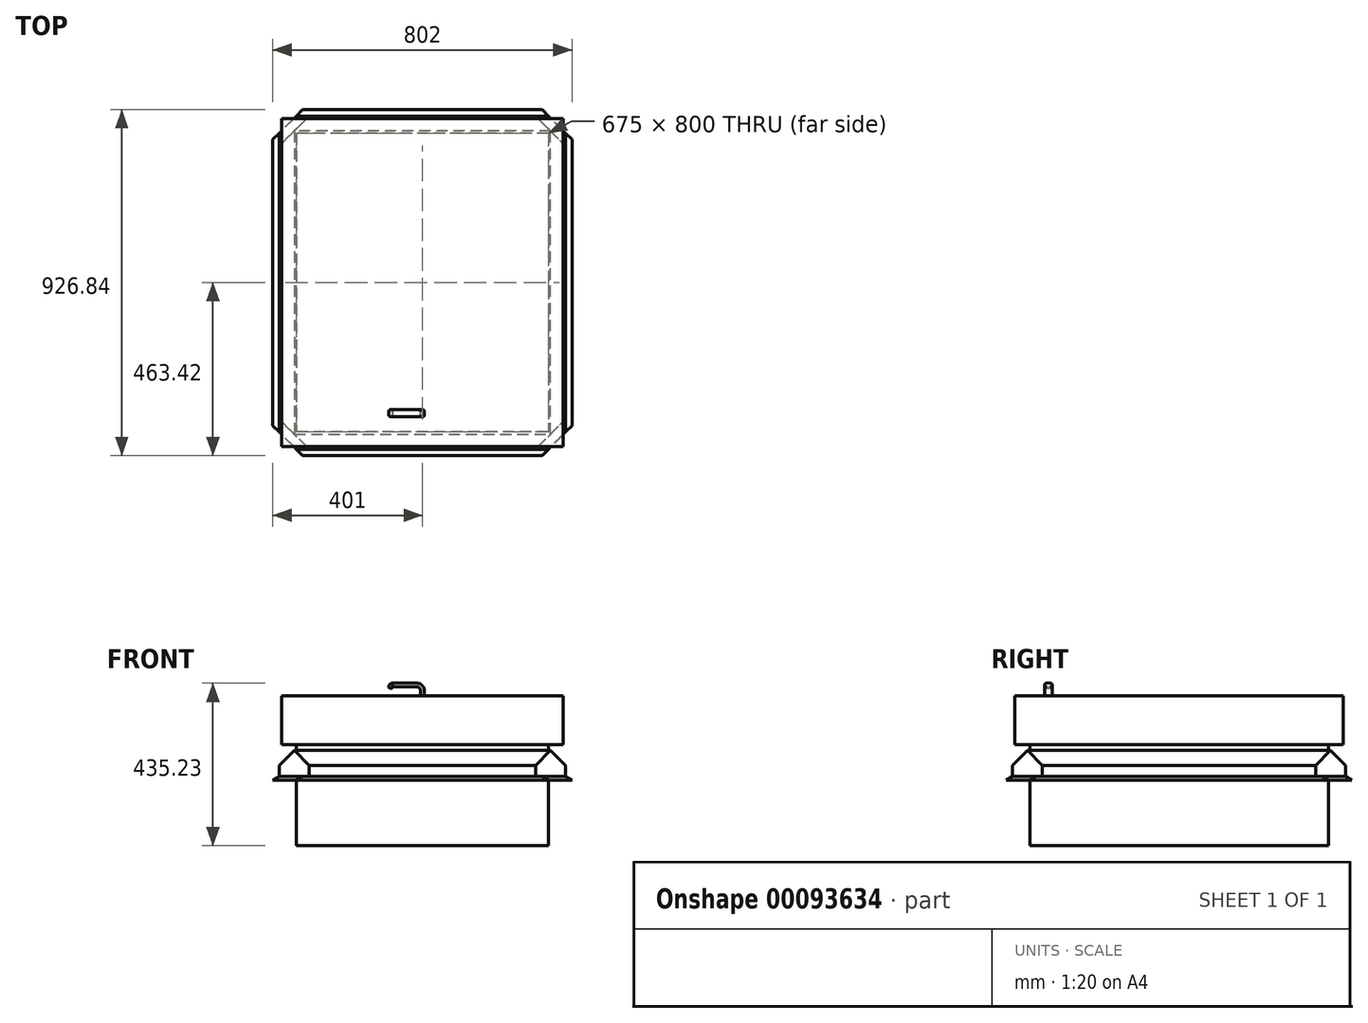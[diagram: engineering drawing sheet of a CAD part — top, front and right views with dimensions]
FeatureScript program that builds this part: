
annotation { "Feature Type Name" : "Feature", "Feature Type Description" : "" }
export const myFeature = defineFeature(function(context is Context, id is Id, definition is map)
    precondition{}
    {
        {
            var Q0;
            Q0=qCreatedBy(makeId("Top.planeOp"),FACE);
            var sketch = newSketch(context, id + "F0", { "sketchPlane" : qUnion([Q0])});
            skLineSegment(sketch, "E0.top", {"start": v(-337.5, 400) * mm, "end": v(337.5, 400) * mm});
            skLineSegment(sketch, "E0.left", {"start": v(-337.5, -400) * mm, "end": v(-337.5, 400) * mm});
            skLineSegment(sketch, "E0.right", {"start": v(337.5, -400) * mm, "end": v(337.5, 400) * mm});
            skPoint(sketch, "E0.middle", {"position": v(0, 0) * mm});
            skPoint(sketch, "E1.endSnap0", {"position": v(-337.5, 0) * mm});
            skLineSegment(sketch, "E2", {"start": v(-337.5, -400) * mm, "end": v(337.5, -400) * mm});
            skPoint(sketch, "E3.start.orphan", {"position": v(-337.5, -825.74) * mm});
            skSolve(sketch);
        }
        {
            var Q0;
            Q0 = qSketchRegion(id + "F0", true);
            extrude(context, id + "F1", {"entities" : qUnion([Q0]), "depth" : 270 * mm});
        }
        {
            var Q0;
            Q0=makeQuery(id+"F1.opExtrude","CAP_FACE",FACE,{"disambiguationData":[OSD([sQuery(id+"F0.wireOp",EDGE,"E0.bottom"),sQuery(id+"F0.wireOp",EDGE,"E0.top"),sQuery(id+"F0.wireOp",EDGE,"E0.left"),sQuery(id+"F0.wireOp",EDGE,"E0.right")])],"isStart":false});
            var sketch = newSketch(context, id + "F2", { "sketchPlane" : qUnion([Q0])});
            skLineSegment(sketch, "E4.top", {"start": v(-377.5, 440) * mm, "end": v(377.5, 440) * mm});
            skPoint(sketch, "E4.middle", {"position": v(0, 0) * mm});
            skPoint(sketch, "E5.orphan", {"position": v(377.5, -440) * mm});
            skLineSegment(sketch, "E6", {"start": v(377.5, -440) * mm, "end": v(-377.5, -440) * mm});
            skLineSegment(sketch, "E7", {"start": v(377.5, -440) * mm, "end": v(377.5, 440) * mm});
            skLineSegment(sketch, "E8", {"start": v(-377.5, 440) * mm, "end": v(-377.5, -440) * mm});
            skSolve(sketch);
        }
        {
            var Q0;
            Q0 = qSketchRegion(id + "F2", true);
            extrude(context, id + "F3", {"entities" : qUnion([Q0]), "operationType" : NewBodyOperationType.ADD, "depth" : 131.76 * mm});
        }
        {
            var Q0;
            Q0=makeQuery(id+"F1.opExtrude","CAP_FACE",FACE,{"disambiguationData":[OSD([sQuery(id+"F0.wireOp",EDGE,"E0.bottom"),sQuery(id+"F0.wireOp",EDGE,"E0.top"),sQuery(id+"F0.wireOp",EDGE,"E0.left"),sQuery(id+"F0.wireOp",EDGE,"E0.right")])],"isStart":true});
            var sketch = newSketch(context, id + "F4", { "sketchPlane" : qUnion([Q0])});
            skLineSegment(sketch, "E9.bottom", {"start": v(-401, -463.42) * mm, "end": v(401, -463.42) * mm});
            skLineSegment(sketch, "E9.left", {"start": v(-401, -463.42) * mm, "end": v(-401, 463.42) * mm});
            skPoint(sketch, "E9.middle", {"position": v(0, 0) * mm});
            skLineSegment(sketch, "E10", {"start": v(-401, 463.42) * mm, "end": v(401, 463.42) * mm});
            skLineSegment(sketch, "E11", {"start": v(401, 463.42) * mm, "end": v(401, -463.42) * mm});
            skSolve(sketch);
        }
        {
            var Q0;
            Q0 = qSketchRegion(id + "F4", true);
            extrude(context, id + "F5", {"entities" : qUnion([Q0]), "operationType" : NewBodyOperationType.ADD, "oppositeDirection" : true, "depth" : 185 * mm, "hasSecondDirection" : true, "secondDirectionOppositeDirection" : true, "secondDirectionDepth" : 175 * mm});
        }
        {
            var Q0;
            Q0=makeQuery(id+"F5.opExtrude","CAP_FACE",FACE,{"disambiguationData":[OSD([sQuery(id+"F4.wireOp",EDGE,"E9.bottom"),sQuery(id+"F4.wireOp",EDGE,"E9.top"),sQuery(id+"F4.wireOp",EDGE,"E9.left"),sQuery(id+"F4.wireOp",EDGE,"E9.right")])],"isStart":false});
            var sketch = newSketch(context, id + "F6", { "sketchPlane" : qUnion([Q0])});
            skLineSegment(sketch, "E12.top", {"start": v(-383.5, 446) * mm, "end": v(383.5, 446) * mm});
            skLineSegment(sketch, "E12.left", {"start": v(-383.5, -446) * mm, "end": v(-383.5, 446) * mm});
            skLineSegment(sketch, "E12.right", {"start": v(383.5, -446) * mm, "end": v(383.5, 446) * mm});
            skPoint(sketch, "E12.middle", {"position": v(0, 0) * mm});
            skPoint(sketch, "E13.orphan", {"position": v(383.5, -446) * mm});
            skLineSegment(sketch, "E14", {"start": v(-383.5, -446) * mm, "end": v(383.5, -446) * mm});
            skSolve(sketch);
        }
        {
            var Q0;
            Q0 = qSketchRegion(id + "F6", true);
            extrude(context, id + "F7", {"entities" : qUnion([Q0]), "operationType" : NewBodyOperationType.ADD, "depth" : 70 * mm});
        }
        {
            var Q0;
            Q0=makeQuery(id+"F7.opExtrude","SWEPT_EDGE",EDGE,{"disambiguationData":[OSD([sQuery(id+"F6.wireOp",EDGE,"E12.bottom"),sQuery(id+"F6.wireOp",EDGE,"E12.right")])]});
            var Q1;
            Q1=makeQuery(id+"F7.opExtrude","SWEPT_EDGE",EDGE,{"disambiguationData":[OSD([sQuery(id+"F6.wireOp",EDGE,"E12.top"),sQuery(id+"F6.wireOp",EDGE,"E12.right")])]});
            var Q2;
            Q2=makeQuery(id+"F7.opExtrude","SWEPT_EDGE",EDGE,{"disambiguationData":[OSD([sQuery(id+"F6.wireOp",EDGE,"E12.top"),sQuery(id+"F6.wireOp",EDGE,"E12.left")])]});
            var Q3;
            Q3=makeQuery(id+"F7.opExtrude","SWEPT_EDGE",EDGE,{"disambiguationData":[OSD([sQuery(id+"F6.wireOp",EDGE,"E12.left"),sQuery(id+"F6.wireOp",EDGE,"E14")])]});
            var Q4;
            Q4=makeQuery(id+"F5.opExtrude","SWEPT_EDGE",EDGE,{"disambiguationData":[OSD([sQuery(id+"F4.wireOp",EDGE,"E9.bottom"),sQuery(id+"F4.wireOp",EDGE,"E9.left")])]});
            var Q5;
            Q5=makeQuery(id+"F5.opExtrude","SWEPT_EDGE",EDGE,{"disambiguationData":[OSD([sQuery(id+"F4.wireOp",EDGE,"E9.left"),sQuery(id+"F4.wireOp",EDGE,"E10")])]});
            var Q6;
            Q6=makeQuery(id+"F5.opExtrude","SWEPT_EDGE",EDGE,{"disambiguationData":[OSD([sQuery(id+"F4.wireOp",EDGE,"E9.bottom"),sQuery(id+"F4.wireOp",EDGE,"E11")])]});
            var Q7;
            Q7=makeQuery(id+"F5.opExtrude","SWEPT_EDGE",EDGE,{"disambiguationData":[OSD([sQuery(id+"F4.wireOp",EDGE,"E10"),sQuery(id+"F4.wireOp",EDGE,"E11")])]});
            chamfer(context, id + "F8", {"entities" : qUnion([Q0, Q1, Q2, Q3, Q4, Q5, Q6, Q7]), "width" : 80 * mm, "tangentPropagation" : true});
        }
        {
            var Q0;
            Q0=makeQuery(id+"F7.opExtrude","CAP_EDGE",EDGE,{"disambiguationData":[OSD([sQuery(id+"F6.wireOp",EDGE,"E12.bottom")])],"isStart":false});
            var Q1;
            Q1=makeQuery(id+"F7.opExtrude","CAP_EDGE",EDGE,{"disambiguationData":[OSD([sQuery(id+"F6.wireOp",EDGE,"E12.right")])],"isStart":false});
            var Q2;
            Q2=makeQuery(id+"F7.opExtrude","CAP_EDGE",EDGE,{"disambiguationData":[OSD([sQuery(id+"F6.wireOp",EDGE,"E12.left")])],"isStart":false});
            var Q3;
            Q3=makeQuery(id+"F7.opExtrude","CAP_EDGE",EDGE,{"disambiguationData":[OSD([sQuery(id+"F6.wireOp",EDGE,"E12.top")])],"isStart":false});
            var Q4;
            Q4=makeQuery(id+"F7.opExtrude","CAP_EDGE",EDGE,{"disambiguationData":[OSD([sQuery(id+"F6.wireOp",EDGE,"E14")])],"isStart":false});
            chamfer(context, id + "F9", {"entities" : qUnion([Q0, Q1, Q2, Q3, Q4]), "width" : 40 * mm, "tangentPropagation" : true});
        }
        {
            var Q0;
            Q0=makeQuery(id+"F5.opExtrude","CAP_EDGE",EDGE,{"disambiguationData":[OSD([sQuery(id+"F4.wireOp",EDGE,"E9.top")])],"isStart":false});
            var Q1;
            Q1=makeQuery(id+"F5.opExtrude","CAP_EDGE",EDGE,{"disambiguationData":[OSD([sQuery(id+"F4.wireOp",EDGE,"E9.left")])],"isStart":false});
            var Q2;
            Q2=makeQuery(id+"F5.opExtrude","CAP_EDGE",EDGE,{"disambiguationData":[OSD([sQuery(id+"F4.wireOp",EDGE,"E9.right")])],"isStart":false});
            var Q3;
            Q3=makeQuery(id+"F5.opExtrude","CAP_EDGE",EDGE,{"disambiguationData":[OSD([sQuery(id+"F4.wireOp",EDGE,"E9.bottom")])],"isStart":false});
            var Q4;
            Q4=makeQuery(id+"F5.opExtrude","CAP_EDGE",EDGE,{"disambiguationData":[OSD([sQuery(id+"F4.wireOp",EDGE,"tBoNisvT-UjQU-eZ0i-RpA4-YddNfWu41SEA")])],"isStart":false});
            var Q5;
            Q5=makeQuery(id+"F5.opExtrude","CAP_EDGE",EDGE,{"disambiguationData":[OSD([sQuery(id+"F4.wireOp",EDGE,"E10")])],"isStart":false});
            var Q6;
            Q6=makeQuery(id+"F5.opExtrude","CAP_EDGE",EDGE,{"disambiguationData":[OSD([sQuery(id+"F4.wireOp",EDGE,"E11")])],"isStart":false});
            chamfer(context, id + "F10", {"entities" : qUnion([Q0, Q1, Q2, Q3, Q4, Q5, Q6]), "chamferType" : ChamferType.TWO_OFFSETS, "width1" : 17 * mm, "oppositeDirection" : false, "width2" : 10 * mm, "tangentPropagation" : true});
        }
        {
            var Q0;
            Q0=qCreatedBy(makeId("Front.planeOp"),FACE);
            cPlane(context, id + "F11", {"entities" : qUnion([Q0]), "cplaneType" : CPlaneType.OFFSET, "offset" : 350 * mm, "width" : 150 * mm, "height" : 150 * mm});
        }
        {
            var Q0;
            Q0=qCreatedBy(id+"F11.planeOp",FACE);
            var sketch = newSketch(context, id + "F12", { "sketchPlane" : qUnion([Q0])});
            skLineSegment(sketch, "E15.0", {"start": v(-554, 401.76) * mm, "end": v(554, 401.76) * mm});
            skLineSegment(sketch, "E16", {"start": v(0, 401.76) * mm, "end": v(0, 415.23) * mm});
            skLineSegment(sketch, "E17", {"start": v(-15, 430.23) * mm, "end": v(-80, 430.23) * mm});
            skLineSegment(sketch, "E18", {"start": v(-85, 425.23) * mm, "end": v(-85, 421.63) * mm});
            skPoint(sketch, "E19.visualSharp", {"position": v(0, 430.23) * mm});
            skArc(sketch, "E19.filletArc", {"start": v(0, 415.23) * mm, "mid": v(-4.4, 425.84) * mm, "end": v(-15, 430.23) * mm});
            skPoint(sketch, "E20.visualSharp", {"position": v(-85, 430.23) * mm});
            skArc(sketch, "E20.filletArc", {"start": v(-80, 430.23) * mm, "mid": v(-83.54, 428.77) * mm, "end": v(-85, 425.23) * mm});
            skSolve(sketch);
        }
        {
            var Q0;
            Q0=makeQuery(id+"F3.opExtrude","CAP_FACE",FACE,{"disambiguationData":[OSD([sQuery(id+"F2.wireOp",EDGE,"E4.bottom"),sQuery(id+"F2.wireOp",EDGE,"E4.top"),sQuery(id+"F2.wireOp",EDGE,"E4.left"),sQuery(id+"F2.wireOp",EDGE,"E4.right")])],"isStart":false});
            var sketch = newSketch(context, id + "F13", { "sketchPlane" : qUnion([Q0])});
            skPoint(sketch, "E21.0", {"position": v(0, -350) * mm});
            skLineSegment(sketch, "E22.bottom", {"start": v(-5, -360) * mm, "end": v(5, -360) * mm});
            skLineSegment(sketch, "E22.top", {"start": v(-5, -340) * mm, "end": v(5, -340) * mm});
            skLineSegment(sketch, "E22.left", {"start": v(-5, -360) * mm, "end": v(-5, -340) * mm});
            skLineSegment(sketch, "E22.right", {"start": v(5, -360) * mm, "end": v(5, -340) * mm});
            skSolve(sketch);
        }
        {
            var Q0;
            Q0=makeQuery(id+"F13.imprint","IMPRINT",FACE,{"disambiguationData":[TD([[makeQuery(id+"F13.imprint","IMPRINT",EDGE,{"derivedFrom":sQuery(id+"F13.wireOp",EDGE,"E22.bottom")}),1.0]])]});
            var Q1;
            Q1=sQuery(id+"F12.wireOp",EDGE,"E16");
            var Q2;
            Q2=sQuery(id+"F12.wireOp",EDGE,"E19.filletArc");
            var Q3;
            Q3=sQuery(id+"F12.wireOp",EDGE,"E17");
            var Q4;
            Q4=sQuery(id+"F12.wireOp",EDGE,"E20.filletArc");
            var Q5;
            Q5=sQuery(id+"F12.wireOp",EDGE,"E18");
            sweep(context, id + "F14", {"operationType" : NewBodyOperationType.ADD, "profiles" : qUnion([Q0]), "path" : qUnion([Q1, Q2, Q3, Q4, Q5])});
        }
        {
            var Q0;
            Q0=makeQuery(id+"F14.opSweep","CAP_EDGE",EDGE,{"disambiguationData":[OSD([sQuery(id+"F12.wireOp",VERTEX,"E18.end"),sQuery(id+"F13.wireOp",EDGE,"E22.right")])],"isStart":false});
            var Q1;
            Q1=makeQuery(id+"F14.opSweep","CAP_EDGE",EDGE,{"disambiguationData":[OSD([sQuery(id+"F12.wireOp",VERTEX,"E18.end"),sQuery(id+"F13.wireOp",EDGE,"E22.bottom")])],"isStart":false});
            var Q2;
            Q2=makeQuery(id+"F14.opSweep","CAP_EDGE",EDGE,{"disambiguationData":[OSD([sQuery(id+"F12.wireOp",VERTEX,"E18.end"),sQuery(id+"F13.wireOp",EDGE,"E22.left")])],"isStart":false});
            var Q3;
            Q3=makeQuery(id+"F14.opSweep","CAP_EDGE",EDGE,{"disambiguationData":[OSD([sQuery(id+"F12.wireOp",VERTEX,"E18.end"),sQuery(id+"F13.wireOp",EDGE,"E22.top")])],"isStart":false});
            fillet(context, id + "F15", {"entities" : qUnion([Q0, Q1, Q2, Q3]), "radius" : 3.5 * mm, "tangentPropagation" : true, "allowEdgeOverflow" : false});
        }
        {
            var Q0;
            Q0=makeQuery(id+"F14.opSweep","SWEPT_EDGE",EDGE,{"disambiguationData":[OSD([sQuery(id+"F12.wireOp",EDGE,"E17"),sQuery(id+"F13.wireOp",EDGE,"E22.bottom"),sQuery(id+"F13.wireOp",EDGE,"E22.right")])]});
            var Q1;
            Q1=makeQuery(id+"F14.opSweep","SWEPT_EDGE",EDGE,{"disambiguationData":[OSD([sQuery(id+"F12.wireOp",EDGE,"E17"),sQuery(id+"F13.wireOp",EDGE,"E22.top"),sQuery(id+"F13.wireOp",EDGE,"E22.right")])]});
            var Q2;
            Q2=makeQuery(id+"F14.opSweep","SWEPT_EDGE",EDGE,{"disambiguationData":[OSD([sQuery(id+"F12.wireOp",EDGE,"E17"),sQuery(id+"F13.wireOp",EDGE,"E22.bottom"),sQuery(id+"F13.wireOp",EDGE,"E22.left")])]});
            var Q3;
            Q3=makeQuery(id+"F14.opSweep","SWEPT_EDGE",EDGE,{"disambiguationData":[OSD([sQuery(id+"F12.wireOp",EDGE,"E17"),sQuery(id+"F13.wireOp",EDGE,"E22.top"),sQuery(id+"F13.wireOp",EDGE,"E22.left")])]});
            fillet(context, id + "F16", {"entities" : qUnion([Q0, Q1, Q2, Q3]), "radius" : 5 * mm, "tangentPropagation" : true, "allowEdgeOverflow" : false});
        }
    });
